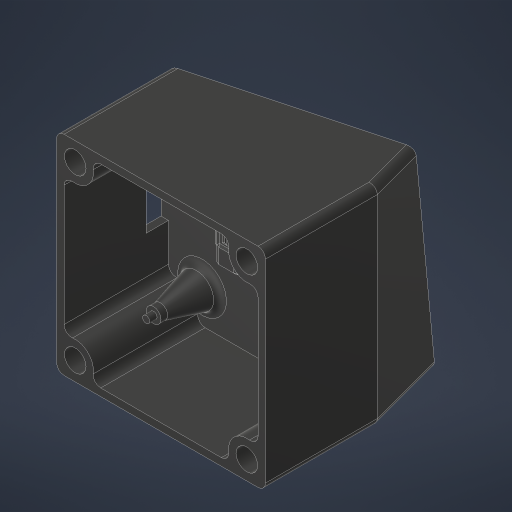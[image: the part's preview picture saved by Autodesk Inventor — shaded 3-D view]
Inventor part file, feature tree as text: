
AUTODESK INVENTOR PART (.ipt)
format: ipt  version: 2023.4 (Build 274418000, 418)  size: 415,232 bytes
history: native  units: in
note: dims shown in document units (in); Inventor stores cm internally (conversion verified against a paired STEP export)
features: extrude x8, projected_geometry x4, hole x2, fillet x2, chamfer x2, mirror x1, shell x1, plane x1, draft x1, sketch x1
ambient origin geometry x8: Origin, YZ Plane, XZ Plane, XY Plane, X Axis, Y Axis, Z Axis, Center Point
bodies: Solid1 (feature_tree)
feature tree (23):
  extrude  "Extrusion1"  Depth=0.2362in
  hole  "Hole1"  [1 undecoded]
  extrude  "Extrusion6"  Depth=0.2362in
  mirror  "Mirror1"
  shell  "Shell1"  Thickness=1.1811in
  extrude  "Extrusion7"  Depth=0.0787in
  fillet  "Fillet1"  Radius=0.3937in
  extrude  "Extrusion2"  Depth=0.2362in
  chamfer  "Chamfer1"  Distance=0.0787in
  extrude  "Extrusion3"  Depth=0.2362in
  extrude  "Extrusion4"  Depth=0.2362in
  plane  "Work Plane1"
  extrude  "Extrusion5"  Depth=0.2362in
  chamfer  "Chamfer2"  Distance=0.1575in
  fillet  "Fillet3"  Radius=0.5906in
  extrude  "Extrusion8"  Depth=0.0787in TaperAngle=75.0deg
  draft  "FaceDraft1"
  hole  "Hole3"  [1 undecoded]
  projected_geometry  "Projected Loop1"
  projected_geometry  "Projected Loop2"
  projected_geometry  "Projected Loop3"
  sketch  "Sketch12"  dims[d0=1.4961in d1=1.4961in d2=1.3386in d3=1.3386in d5=1.1811in d6=0.0in d7=0.0787in d8=0.3937in d9=1.811in d10=0.2283in d11=0.2362in d12=0.385in d13=0.0787in d14=0.5635in d15=0.315in d16=0.8108in d17=0.0787in d18=0.1575in d19=0.1575in d20=0.1575in d21=0.1575in d22=0.5906in d23=0.0in d24=0.1181in d25=0.0787in d26=75.0deg d27=0.0748in d28=0.0748in d29=0.0748in d30=0.0748in d31=0.0787in d32=0.0in d33=0.4724in d34=0.2362in d35=0.0787in d36=1.1811in d37=0.0in d42=0.1969in d43=0.0in d44=0.0197in d45=0.0787in d46=0.481in d47=0.2283in d48=0.2283in d49=0.1969in d50=1.0in d51=0.2756in d52=0.0in d61=0.0787in d62=15.0deg d63=0.3937in d64=0.0in d65=0.0591in d66=0.1969in d67=0.5906in d68=45.0deg d69=45.0deg d70=0.5906in d71=0.1843in d72=0.0591in d73=0.0591in d74=1.5748in d75=1.5748in d76=0.2283in d77=0.2283in d80=0.315in d81=0.0in d82=0.2283in d83=0.0515in d86=0.2283in d87=0.2362in d88=0.385in d89=0.0787in d90=0.5635in d91=0.2362in d92=0.0in d93=0.5in d94=1.5in d96=0.375in d60=0.0in]
  projected_geometry  "Project Cut Edges1"
note: 2 required parameter values undecoded (feature->parameter linkage not recoverable at this tier; creation-order binding heuristic only, values carry confidence <= 0.55)
